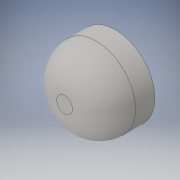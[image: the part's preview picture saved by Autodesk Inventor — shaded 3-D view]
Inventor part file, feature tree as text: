
AUTODESK INVENTOR PART (.ipt)
format: ipt  version: 2016 (Build 200138000, 138)  size: 136,192 bytes
history: native  units: in
note: dims shown in document units (in); Inventor stores cm internally (conversion verified against a paired STEP export)
features: extrude x2, sketch x2, fillet x1
ambient origin geometry x8: Origin, YZ Plane, XZ Plane, XY Plane, X Axis, Y Axis, Z Axis, Center Point
bodies: Solid1 (feature_tree)
feature tree (5):
  extrude  "Extrusion1"  Depth=1.0in TaperAngle=0.0deg
  fillet  "Fillet1"  Radius=0.62in
  extrude  "Extrusion2"  Depth=1.03in
  sketch  "Sketch1"  dims[d0=1.55in d1=1.0in d2=0.0in d3=0.62in]
  sketch  "Sketch2"  dims[d4=1.03in d5=1.03in d6=0.515in d8=0.515in d9=0.5in d10=0.0in]
